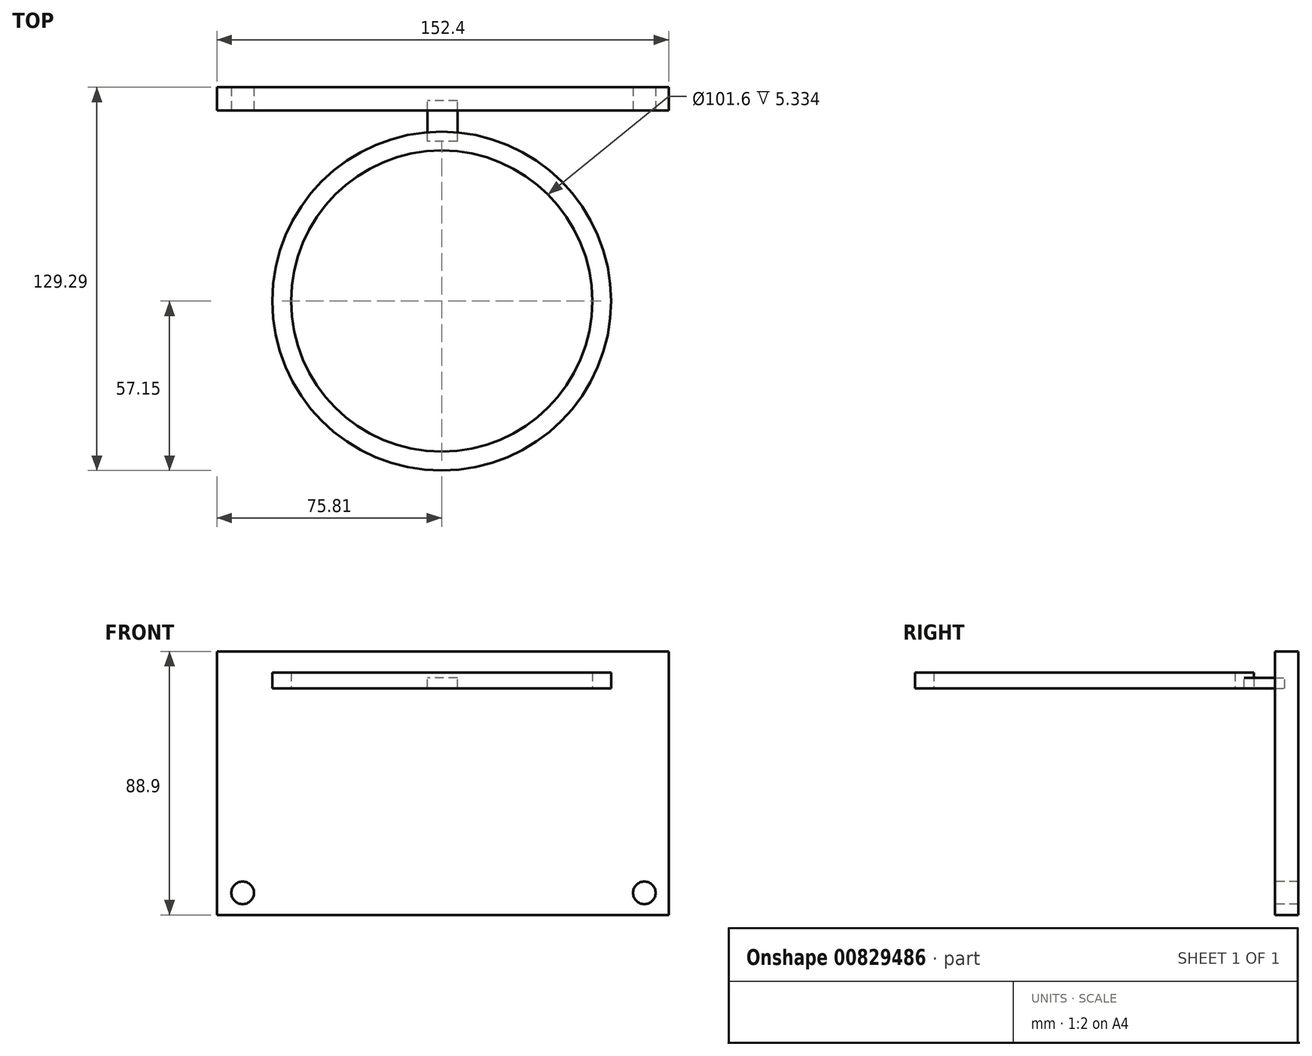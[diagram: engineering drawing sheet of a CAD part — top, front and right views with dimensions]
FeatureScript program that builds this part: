
annotation { "Feature Type Name" : "Feature", "Feature Type Description" : "" }
export const myFeature = defineFeature(function(context is Context, id is Id, definition is map)
    precondition{}
    {
        {
            var Q0;
            Q0=qCreatedBy(makeId("Top.planeOp"),FACE);
            var sketch = newSketch(context, id + "F0", { "sketchPlane" : qUnion([Q0])});
            skCircle(sketch, "E0", {"center": v(0, 0) * mm, "radius": 57.15 * mm});
            skCircle(sketch, "E1", {"center": v(0, 0) * mm, "radius": 50.8 * mm});
            skSolve(sketch);
        }
        {
            var Q0;
            Q0 = qSketchRegion(id + "F0", true);
            extrude(context, id + "F1", {"entities" : qUnion([Q0]), "depth" : 5.33 * mm, "offsetDistance" : 25.4 * mm});
        }
        {
            var Q0;
            Q0=qCreatedBy(makeId("Front.planeOp"),FACE);
            var sketch = newSketch(context, id + "F2", { "sketchPlane" : qUnion([Q0])});
            skLineSegment(sketch, "E2.bottom", {"start": v(-75.8, -76.45) * mm, "end": v(76.6, -76.45) * mm});
            skLineSegment(sketch, "E2.top", {"start": v(-75.8, 12.45) * mm, "end": v(76.6, 12.45) * mm});
            skLineSegment(sketch, "E2.left", {"start": v(-75.8, -76.45) * mm, "end": v(-75.8, 12.45) * mm});
            skLineSegment(sketch, "E2.right", {"start": v(76.6, -76.45) * mm, "end": v(76.6, 12.45) * mm});
            skCircle(sketch, "E3", {"center": v(-67.13, -69) * mm, "radius": 3.81 * mm});
            skCircle(sketch, "E4", {"center": v(68.36, -69) * mm, "radius": 3.81 * mm});
            skSolve(sketch);
        }
        {
            var Q0;
            Q0 = qSketchRegion(id + "F2", true);
            extrude(context, id + "F3", {"entities" : qUnion([Q0]), "oppositeDirection" : true, "depth" : 72.14 * mm, "offsetDistance" : 25.4 * mm, "hasSecondDirection" : true, "secondDirectionOppositeDirection" : true, "secondDirectionDepth" : 64.26 * mm});
        }
        {
            var Q0;
            Q0=qCreatedBy(makeId("Right.planeOp"),FACE);
            var sketch = newSketch(context, id + "F4", { "sketchPlane" : qUnion([Q0])});
            skLineSegment(sketch, "E5.bottom", {"start": v(53.9, 0) * mm, "end": v(67.55, 0) * mm});
            skLineSegment(sketch, "E5.top", {"start": v(53.9, 3.54) * mm, "end": v(67.55, 3.54) * mm});
            skLineSegment(sketch, "E5.left", {"start": v(53.9, 0) * mm, "end": v(53.9, 3.54) * mm});
            skLineSegment(sketch, "E5.right", {"start": v(67.55, 0) * mm, "end": v(67.55, 3.54) * mm});
            skSolve(sketch);
        }
        {
            var Q0;
            Q0 = qSketchRegion(id + "F4", true);
            extrude(context, id + "F5", {"entities" : qUnion([Q0]), "depth" : 5.33 * mm, "offsetDistance" : 25.4 * mm, "hasSecondDirection" : true, "secondDirectionOppositeDirection" : true, "secondDirectionDepth" : 4.83 * mm});
        }
    });
